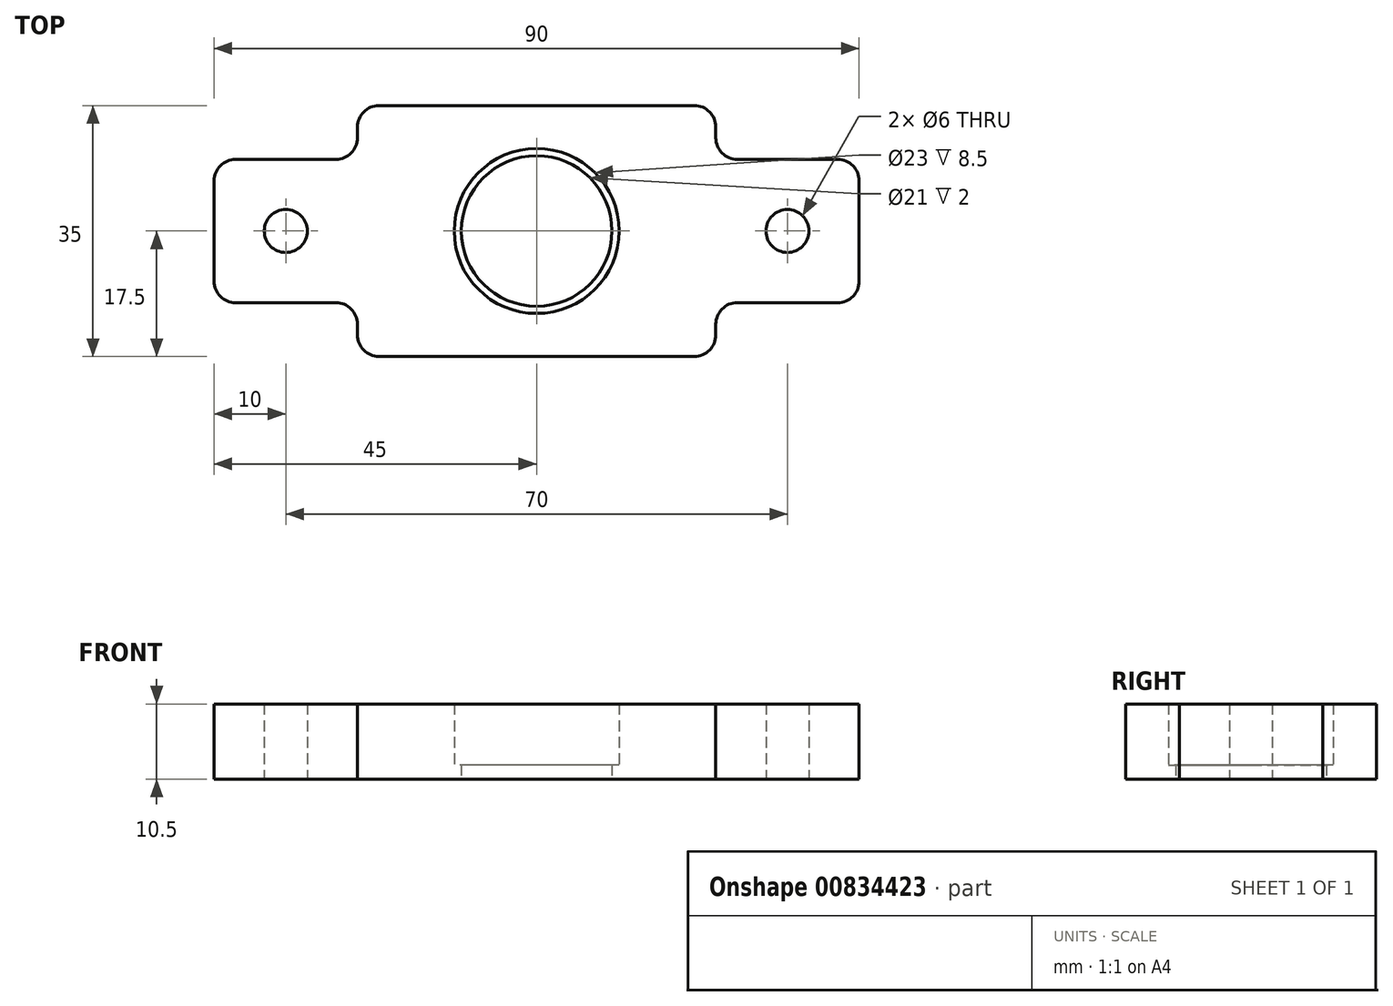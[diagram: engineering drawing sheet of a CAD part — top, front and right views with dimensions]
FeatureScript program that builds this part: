
annotation { "Feature Type Name" : "Feature", "Feature Type Description" : "" }
export const myFeature = defineFeature(function(context is Context, id is Id, definition is map)
    precondition{}
    {
        {
            var Q0;
            Q0=qCreatedBy(makeId("Top.planeOp"),FACE);
            var sketch = newSketch(context, id + "F0", { "sketchPlane" : qUnion([Q0])});
            skLineSegment(sketch, "E0.bottom", {"start": v(-25, 17.5) * mm, "end": v(25, 17.5) * mm});
            skLineSegment(sketch, "E0.top", {"start": v(-25, -17.5) * mm, "end": v(25, -17.5) * mm});
            skLineSegment(sketch, "E0.left", {"start": v(-25, 17.5) * mm, "end": v(-25, -17.5) * mm});
            skLineSegment(sketch, "E0.right", {"start": v(25, 17.5) * mm, "end": v(25, -17.5) * mm});
            skPoint(sketch, "E0.middle", {"position": v(0, 0) * mm});
            skLineSegment(sketch, "E1.bottom", {"start": v(-25, 10) * mm, "end": v(-45, 10) * mm});
            skLineSegment(sketch, "E1.top", {"start": v(-25, -10) * mm, "end": v(-45, -10) * mm});
            skLineSegment(sketch, "E1.left", {"start": v(-25, 10) * mm, "end": v(-25, -10) * mm});
            skLineSegment(sketch, "E1.right", {"start": v(-45, 10) * mm, "end": v(-45, -10) * mm});
            skLineSegment(sketch, "E2.MirrorCS", {"start": v(25, 10) * mm, "end": v(45, 10) * mm});
            skLineSegment(sketch, "E3.MirrorCS", {"start": v(45, 10) * mm, "end": v(45, -10) * mm});
            skLineSegment(sketch, "E4.MirrorCS", {"start": v(25, -10) * mm, "end": v(45, -10) * mm});
            skCircle(sketch, "E5", {"center": v(0, 0) * mm, "radius": 11.5 * mm});
            skCircle(sketch, "E6", {"center": v(0, 0) * mm, "radius": 10.5 * mm});
            skCircle(sketch, "E7", {"center": v(-35, 0) * mm, "radius": 3 * mm});
            skPoint(sketch, "E7.centerSnap0", {"position": v(-35, 10) * mm});
            skPoint(sketch, "E7.centerSnap1", {"position": v(-45, 0) * mm});
            skCircle(sketch, "E8.MirrorC", {"center": v(35, 0) * mm, "radius": 3 * mm});
            skSolve(sketch);
        }
        {
            var Q0;
            Q0 = qSketchRegion(id + "F0", true);
            extrude(context, id + "F1", {"entities" : qUnion([Q0]), "depth" : 10.5 * mm, "offsetDistance" : 25 * mm});
        }
        {
            var Q0;
            Q0=makeQuery(id+"F0.imprint","IMPRINT",FACE,{"disambiguationData":[TD([[makeQuery(id+"F0.imprint","IMPRINT",EDGE,{"derivedFrom":sQuery(id+"F0.wireOp",EDGE,"E5")}),1.0]])]});
            extrude(context, id + "F2", {"entities" : qUnion([Q0]), "operationType" : NewBodyOperationType.ADD, "depth" : 2 * mm, "offsetDistance" : 25 * mm});
        }
        {
            var Q0;
            Q0=makeQuery(id+"F1.opExtrude","SWEPT_EDGE",EDGE,{"disambiguationData":[OSD([sQuery(id+"F0.wireOp",EDGE,"E0.left"),sQuery(id+"F0.wireOp",EDGE,"E1.top"),sQuery(id+"F0.wireOp",EDGE,"E1.left")])]});
            var Q1;
            Q1=makeQuery(id+"F1.opExtrude","SWEPT_EDGE",EDGE,{"disambiguationData":[OSD([sQuery(id+"F0.wireOp",EDGE,"E0.left"),sQuery(id+"F0.wireOp",EDGE,"E1.bottom"),sQuery(id+"F0.wireOp",EDGE,"E1.left")])]});
            var Q2;
            Q2=makeQuery(id+"F1.opExtrude","SWEPT_EDGE",EDGE,{"disambiguationData":[OSD([sQuery(id+"F0.wireOp",EDGE,"E0.right"),sQuery(id+"F0.wireOp",EDGE,"E2.MirrorCS")])]});
            var Q3;
            Q3=makeQuery(id+"F1.opExtrude","SWEPT_EDGE",EDGE,{"disambiguationData":[OSD([sQuery(id+"F0.wireOp",EDGE,"E0.right"),sQuery(id+"F0.wireOp",EDGE,"E4.MirrorCS")])]});
            var Q4;
            Q4=makeQuery(id+"F1.opExtrude","SWEPT_EDGE",EDGE,{"disambiguationData":[OSD([sQuery(id+"F0.wireOp",EDGE,"E0.bottom"),sQuery(id+"F0.wireOp",EDGE,"E0.right")])]});
            var Q5;
            Q5=makeQuery(id+"F1.opExtrude","SWEPT_EDGE",EDGE,{"disambiguationData":[OSD([sQuery(id+"F0.wireOp",EDGE,"E0.top"),sQuery(id+"F0.wireOp",EDGE,"E0.right")])]});
            var Q6;
            Q6=makeQuery(id+"F1.opExtrude","SWEPT_EDGE",EDGE,{"disambiguationData":[OSD([sQuery(id+"F0.wireOp",EDGE,"E0.top"),sQuery(id+"F0.wireOp",EDGE,"E0.left")])]});
            var Q7;
            Q7=makeQuery(id+"F1.opExtrude","SWEPT_EDGE",EDGE,{"disambiguationData":[OSD([sQuery(id+"F0.wireOp",EDGE,"E0.bottom"),sQuery(id+"F0.wireOp",EDGE,"E0.left")])]});
            var Q8;
            Q8=makeQuery(id+"F1.opExtrude","SWEPT_EDGE",EDGE,{"disambiguationData":[OSD([sQuery(id+"F0.wireOp",EDGE,"E1.bottom"),sQuery(id+"F0.wireOp",EDGE,"E1.right")])]});
            var Q9;
            Q9=makeQuery(id+"F1.opExtrude","SWEPT_EDGE",EDGE,{"disambiguationData":[OSD([sQuery(id+"F0.wireOp",EDGE,"E1.top"),sQuery(id+"F0.wireOp",EDGE,"E1.right")])]});
            var Q10;
            Q10=makeQuery(id+"F1.opExtrude","SWEPT_EDGE",EDGE,{"disambiguationData":[OSD([sQuery(id+"F0.wireOp",EDGE,"E3.MirrorCS"),sQuery(id+"F0.wireOp",EDGE,"E4.MirrorCS")])]});
            var Q11;
            Q11=makeQuery(id+"F1.opExtrude","SWEPT_EDGE",EDGE,{"disambiguationData":[OSD([sQuery(id+"F0.wireOp",EDGE,"E2.MirrorCS"),sQuery(id+"F0.wireOp",EDGE,"E3.MirrorCS")])]});
            fillet(context, id + "F3", {"entities" : qUnion([Q0, Q1, Q2, Q3, Q4, Q5, Q6, Q7, Q8, Q9, Q10, Q11]), "radius" : 3 * mm, "tangentPropagation" : true, "allowEdgeOverflow" : false});
        }
    });
